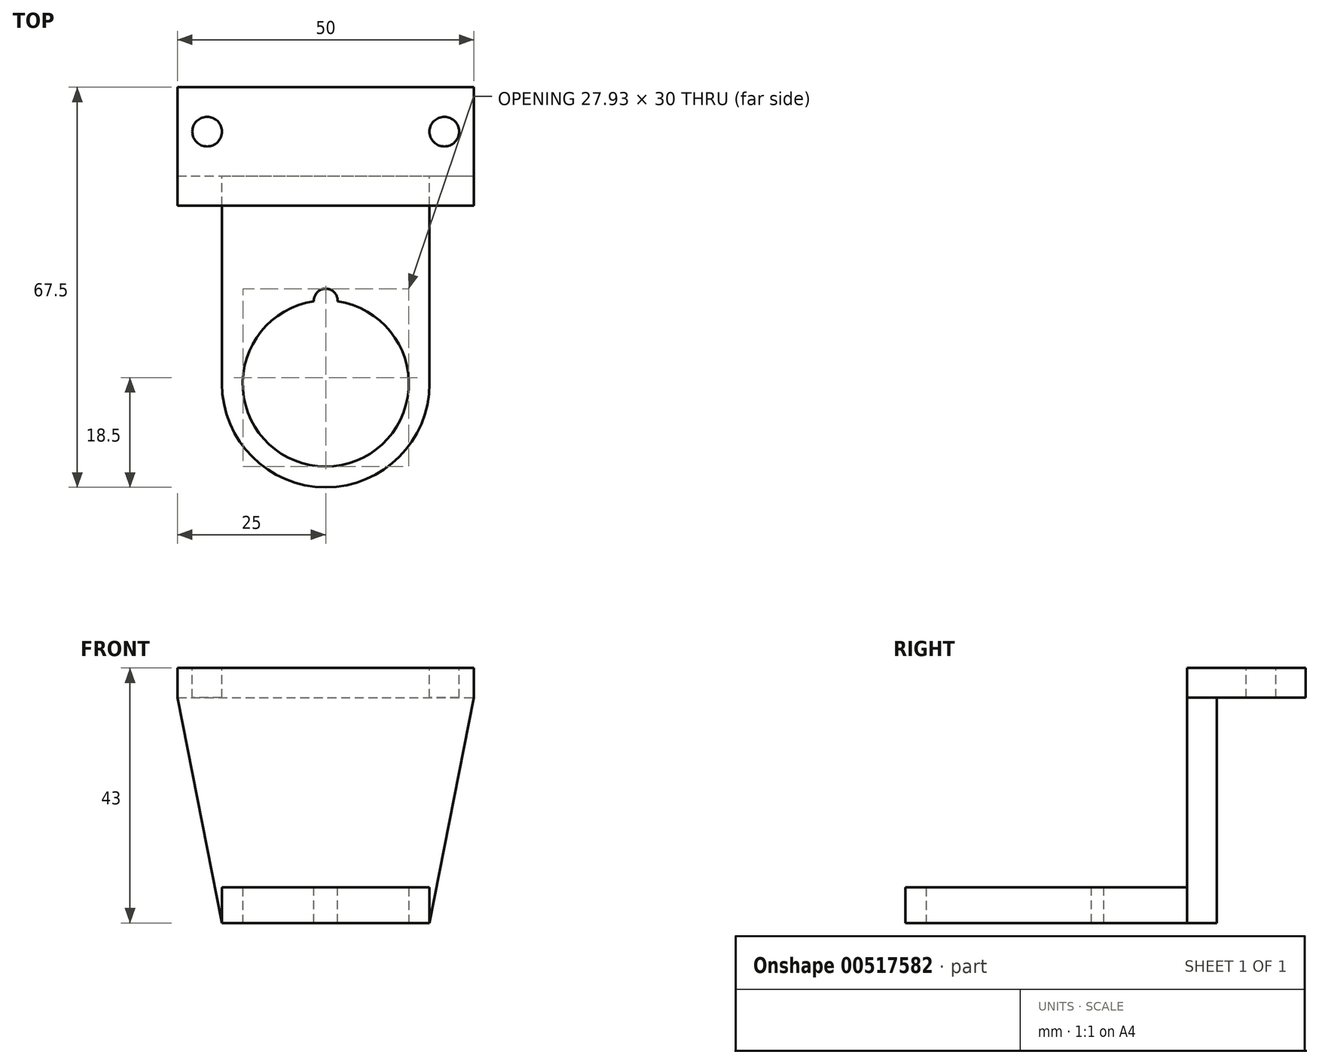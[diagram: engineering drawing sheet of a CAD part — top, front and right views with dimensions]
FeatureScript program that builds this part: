
annotation { "Feature Type Name" : "Feature", "Feature Type Description" : "" }
export const myFeature = defineFeature(function(context is Context, id is Id, definition is map)
    precondition{}
    {
        {
            var Q0;
            Q0=qCreatedBy(makeId("Front.planeOp"),FACE);
            var sketch = newSketch(context, id + "F0", { "sketchPlane" : qUnion([Q0])});
            skLineSegment(sketch, "E0.bottom", {"start": v(-25, 38) * mm, "end": v(25, 38) * mm});
            skLineSegment(sketch, "E0.top", {"start": v(-25, 43) * mm, "end": v(25, 43) * mm});
            skLineSegment(sketch, "E0.left", {"start": v(-25, 38) * mm, "end": v(-25, 43) * mm});
            skLineSegment(sketch, "E0.right", {"start": v(25, 38) * mm, "end": v(25, 43) * mm});
            skSolve(sketch);
        }
        {
            var Q0;
            Q0=makeQuery(id+"F0.imprint","IMPRINT",FACE,{"disambiguationData":[TD([[makeQuery(id+"F0.imprint","IMPRINT",EDGE,{"derivedFrom":sQuery(id+"F0.wireOp",EDGE,"E0.bottom")}),1.0]])]});
            extrude(context, id + "F1", {"entities" : qUnion([Q0]), "depth" : 15 * mm, "offsetDistance" : 25 * mm});
        }
        {
            var Q0;
            Q0=makeQuery(id+"F1.opExtrude","SWEPT_FACE",FACE,{"disambiguationData":[OSD([sQuery(id+"F0.wireOp",EDGE,"E0.top")])]});
            var sketch = newSketch(context, id + "F2", { "sketchPlane" : qUnion([Q0])});
            skCircle(sketch, "E1", {"center": v(-20, -7.5) * mm, "radius": 2.5 * mm});
            skCircle(sketch, "E2", {"center": v(20, -7.5) * mm, "radius": 2.5 * mm});
            skSolve(sketch);
        }
        {
            var Q0;
            Q0=makeQuery(id+"F2.imprint","IMPRINT",FACE,{"disambiguationData":[TD([[makeQuery(id+"F2.imprint","IMPRINT",EDGE,{"derivedFrom":sQuery(id+"F2.wireOp",EDGE,"E1")}),1.0]])]});
            var Q1;
            Q1=makeQuery(id+"F2.imprint","IMPRINT",FACE,{"disambiguationData":[TD([[makeQuery(id+"F2.imprint","IMPRINT",EDGE,{"derivedFrom":sQuery(id+"F2.wireOp",EDGE,"E2")}),1.0]])]});
            extrude(context, id + "F3", {"entities" : qUnion([Q0, Q1]), "operationType" : NewBodyOperationType.REMOVE, "oppositeDirection" : true, "depth" : 25 * mm, "offsetDistance" : 25 * mm});
        }
        {
            var Q0;
            Q0=makeQuery(id+"F1.opExtrude","CAP_FACE",FACE,{"disambiguationData":[OSD([sQuery(id+"F0.wireOp",EDGE,"E0.bottom"),sQuery(id+"F0.wireOp",EDGE,"E0.top"),sQuery(id+"F0.wireOp",EDGE,"E0.left"),sQuery(id+"F0.wireOp",EDGE,"E0.right")])],"isStart":false});
            var sketch = newSketch(context, id + "F4", { "sketchPlane" : qUnion([Q0])});
            skLineSegment(sketch, "E3", {"start": v(-25, 38) * mm, "end": v(-17.5, 0) * mm});
            skLineSegment(sketch, "E4", {"start": v(-17.5, 0) * mm, "end": v(17.5, 0) * mm});
            skLineSegment(sketch, "E5", {"start": v(17.5, 0) * mm, "end": v(25, 38) * mm});
            skLineSegment(sketch, "E6", {"start": v(25, 38) * mm, "end": v(25, 43) * mm});
            skLineSegment(sketch, "E7", {"start": v(25, 43) * mm, "end": v(-25, 43) * mm});
            skLineSegment(sketch, "E8", {"start": v(-25, 43) * mm, "end": v(-25, 38) * mm});
            skSolve(sketch);
        }
        {
            var Q0;
            Q0=makeQuery(id+"F4.imprint","IMPRINT",FACE,{"disambiguationData":[TD([[makeQuery(id+"F4.imprint","IMPRINT",EDGE,{"derivedFrom":sQuery(id+"F4.wireOp",EDGE,"E6")}),1.0]])]});
            var Q1;
            Q1=makeQuery(id+"F4.imprint","IMPRINT",FACE,{"disambiguationData":[TD([[makeQuery(id+"F4.imprint","IMPRINT",EDGE,{"derivedFrom":sQuery(id+"F4.wireOp",EDGE,"E3")}),1.0]])]});
            extrude(context, id + "F5", {"entities" : qUnion([Q0, Q1]), "operationType" : NewBodyOperationType.ADD, "depth" : 5 * mm, "offsetDistance" : 25 * mm});
        }
        {
            var Q0;
            Q0=makeQuery(id+"F5.opExtrude","SWEPT_FACE",FACE,{"disambiguationData":[OSD([sQuery(id+"F4.wireOp",EDGE,"E4")])]});
            var sketch = newSketch(context, id + "F6", { "sketchPlane" : qUnion([Q0])});
            skLineSegment(sketch, "E9.bottom", {"start": v(17.5, 15) * mm, "end": v(-17.5, 15) * mm});
            skLineSegment(sketch, "E9.left", {"start": v(17.5, 15) * mm, "end": v(17.5, 50) * mm});
            skLineSegment(sketch, "E9.right", {"start": v(-17.5, 15) * mm, "end": v(-17.5, 50) * mm});
            skCircle(sketch, "E10", {"center": v(0, 50) * mm, "radius": 14 * mm});
            skPoint(sketch, "E10.centerSnap0", {"position": v(0, 15) * mm});
            skArc(sketch, "E11", {"start": v(17.5, 50) * mm, "mid": v(0, 67.5) * mm, "end": v(-17.5, 50) * mm});
            skPoint(sketch, "E9.top.end.orphan", {"position": v(-17.5, 70) * mm});
            skPoint(sketch, "E9.top.start.orphan", {"position": v(17.5, 70) * mm});
            skSolve(sketch);
        }
        {
            var Q0;
            Q0=makeQuery(id+"F6.imprint","IMPRINT",FACE,{"disambiguationData":[TD([[makeQuery(id+"F6.imprint","IMPRINT",EDGE,{"derivedFrom":sQuery(id+"F6.wireOp",EDGE,"E10")}),-1.0]])]});
            extrude(context, id + "F7", {"entities" : qUnion([Q0]), "operationType" : NewBodyOperationType.ADD, "oppositeDirection" : true, "depth" : 6 * mm, "offsetDistance" : 25 * mm});
        }
        {
            var Q0;
            Q0=makeQuery(id+"F7.opExtrude","CAP_FACE",FACE,{"disambiguationData":[OSD([sQuery(id+"F4.wireOp",EDGE,"E4"),sQuery(id+"F6.wireOp",EDGE,"E9.left"),sQuery(id+"F6.wireOp",EDGE,"E9.right"),sQuery(id+"F6.wireOp",EDGE,"E10"),sQuery(id+"F6.wireOp",EDGE,"E11")])],"isStart":false});
            var sketch = newSketch(context, id + "F8", { "sketchPlane" : qUnion([Q0])});
            skCircle(sketch, "E12", {"center": v(0, -36) * mm, "radius": 2 * mm});
            skSolve(sketch);
        }
        {
            var Q0;
            {var subQ0=sQuery(id+"F8.wireOp",EDGE,"E12");var subQ1=makeQuery(id+"F7.opExtrude","CAP_EDGE",EDGE,{"disambiguationData":[OSD([sQuery(id+"F6.wireOp",EDGE,"E10")])],"isStart":false});var subQ2=makeQuery(id+"F8.imprint","INTERSECT",VERTEX,{"disambiguationData":[OD(0.0)],"derivedFrom":[subQ1,subQ0]});Q0=makeQuery(id+"F8.imprint","IMPRINT",FACE,{"disambiguationData":[TD([[makeQuery(id+"F8.imprint","IMPRINT",EDGE,{"disambiguationData":[TD([[subQ2,1.0]])],"derivedFrom":subQ0}),1.0]])]});}
            extrude(context, id + "F9", {"entities" : qUnion([Q0]), "operationType" : NewBodyOperationType.REMOVE, "oppositeDirection" : true, "depth" : 25 * mm, "offsetDistance" : 25 * mm});
        }
    });
